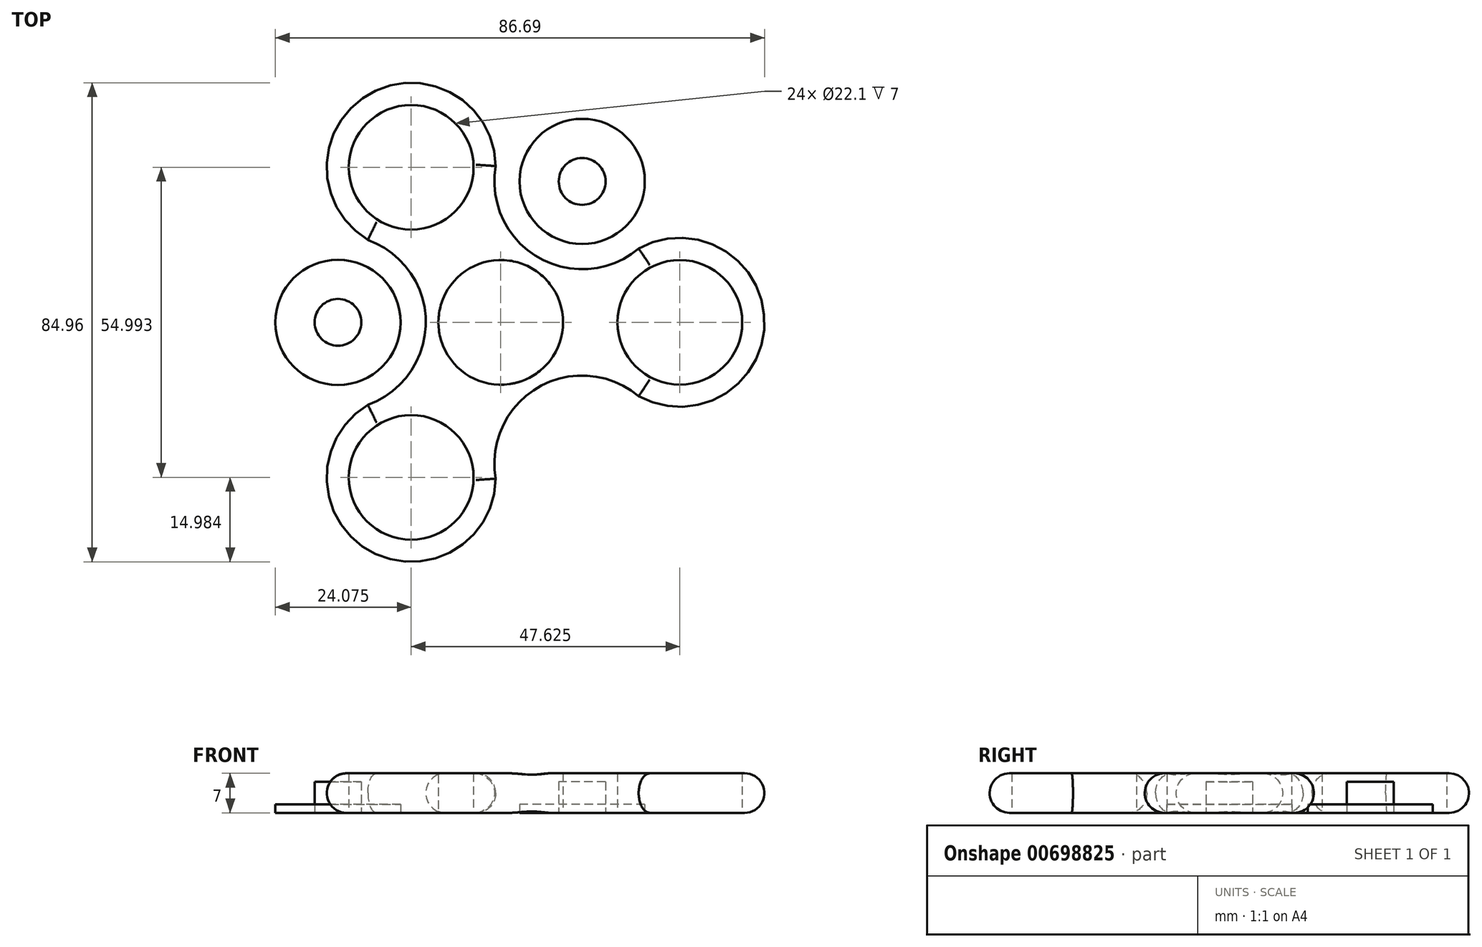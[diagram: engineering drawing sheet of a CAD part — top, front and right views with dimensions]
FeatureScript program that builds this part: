
annotation { "Feature Type Name" : "Feature", "Feature Type Description" : "" }
export const myFeature = defineFeature(function(context is Context, id is Id, definition is map)
    precondition{}
    {
        {
            var Q0;
            Q0=qCreatedBy(makeId("Top.planeOp"),FACE);
            var sketch = newSketch(context, id + "F0", { "sketchPlane" : qUnion([Q0])});
            skCircle(sketch, "E0", {"center": v(0, 0) * mm, "radius": 11.05 * mm});
            skCircle(sketch, "E1", {"center": v(0, 0) * mm, "radius": 14.99 * mm});
            skLineSegment(sketch, "E2", {"start": v(-11.05, 0) * mm, "end": v(-14.99, 0) * mm, "construction": true});
            skLineSegment(sketch, "E3.0", {"start": v(29.97, 0) * mm, "end": v(-14.99, -25.96) * mm, "construction": true});
            skLineSegment(sketch, "E3.1", {"start": v(-14.99, -25.96) * mm, "end": v(-14.99, 25.96) * mm, "construction": true});
            skLineSegment(sketch, "E3.2", {"start": v(-14.99, 25.96) * mm, "end": v(29.97, 0) * mm, "construction": true});
            skPoint(sketch, "E3.0.midPoint", {"position": v(7.5, -12.98) * mm});
            skLineSegment(sketch, "E4", {"start": v(0, 0) * mm, "end": v(7.5, 12.98) * mm, "construction": true});
            skLineSegment(sketch, "E5", {"start": v(0, 0) * mm, "end": v(7.5, -12.98) * mm, "construction": true});
            skLineSegment(sketch, "E6", {"start": v(0, 0) * mm, "end": v(-14.99, 0) * mm, "construction": true});
            skCircle(sketch, "E7", {"center": v(31.75, 0) * mm, "radius": 11.05 * mm});
            skLineSegment(sketch, "E8", {"start": v(42.8, 0) * mm, "end": v(46.74, 0) * mm, "construction": true});
            skLineSegment(sketch, "E9", {"start": v(31.75, 14.99) * mm, "end": v(31.75, -14.99) * mm, "construction": true});
            skLineSegment(sketch, "E10", {"start": v(0, 0) * mm, "end": v(31.75, 0) * mm, "construction": true});
            skCircle(sketch, "E11", {"center": v(31.75, 0) * mm, "radius": 14.99 * mm});
            skLineSegment(sketch, "E12", {"start": v(0, 0) * mm, "end": v(-15.88, 27.5) * mm, "construction": true});
            skCircle(sketch, "E13", {"center": v(-15.87, 27.5) * mm, "radius": 14.99 * mm});
            skCircle(sketch, "E14", {"center": v(-15.87, 27.5) * mm, "radius": 11.05 * mm});
            skLineSegment(sketch, "E15", {"start": v(-28.85, 20) * mm, "end": v(-2.9, 34.99) * mm, "construction": true});
            skLineSegment(sketch, "E16", {"start": v(-14.99, 0) * mm, "end": v(7.5, 12.98) * mm, "construction": true});
            skLineSegment(sketch, "E17", {"start": v(-14.99, 0) * mm, "end": v(7.5, -12.98) * mm, "construction": true});
            skLineSegment(sketch, "E18", {"start": v(7.5, -12.98) * mm, "end": v(7.5, 12.98) * mm, "construction": true});
            skLineSegment(sketch, "E19", {"start": v(0, 0) * mm, "end": v(-15.87, -27.5) * mm, "construction": true});
            skCircle(sketch, "E20", {"center": v(-15.87, -27.5) * mm, "radius": 14.99 * mm});
            skCircle(sketch, "E21", {"center": v(-15.87, -27.5) * mm, "radius": 11.05 * mm});
            skLineSegment(sketch, "E22", {"start": v(-2.9, -34.99) * mm, "end": v(-28.85, -20) * mm, "construction": true});
            skLineSegment(sketch, "E23", {"start": v(-28.85, 20) * mm, "end": v(-28.85, -20) * mm});
            skLineSegment(sketch, "E24", {"start": v(-2.9, -34.99) * mm, "end": v(31.75, -14.99) * mm});
            skLineSegment(sketch, "E25", {"start": v(31.75, 14.99) * mm, "end": v(-2.9, 34.99) * mm});
            skPoint(sketch, "E26", {"position": v(-28.85, 0) * mm});
            skPoint(sketch, "E27", {"position": v(14.43, 24.99) * mm});
            skCircle(sketch, "E28", {"center": v(-28.85, 0) * mm, "radius": 15.56 * mm});
            skCircle(sketch, "E29", {"center": v(14.43, 24.99) * mm, "radius": 15.56 * mm});
            skPoint(sketch, "E30", {"position": v(14.43, -24.99) * mm});
            skCircle(sketch, "E31", {"center": v(14.43, -24.99) * mm, "radius": 15.56 * mm});
            skSolve(sketch);
        }
        {
            var Q0;
            Q0=makeQuery(id+"F0.imprint","IMPRINT",FACE,{"disambiguationData":[TD([[makeQuery(id+"F0.imprint","IMPRINT",EDGE,{"derivedFrom":sQuery(id+"F0.wireOp",EDGE,"E14")}),-1.0]])]});
            var Q1;
            Q1=makeQuery(id+"F0.imprint","IMPRINT",FACE,{"disambiguationData":[TD([[makeQuery(id+"F0.imprint","IMPRINT",EDGE,{"derivedFrom":sQuery(id+"F0.wireOp",EDGE,"E1")}),-1.0]])]});
            var Q2;
            Q2=makeQuery(id+"F0.imprint","IMPRINT",FACE,{"disambiguationData":[TD([[makeQuery(id+"F0.imprint","IMPRINT",EDGE,{"derivedFrom":sQuery(id+"F0.wireOp",EDGE,"E7")}),-1.0]])]});
            var Q3;
            Q3=makeQuery(id+"F0.imprint","IMPRINT",FACE,{"disambiguationData":[TD([[makeQuery(id+"F0.imprint","IMPRINT",EDGE,{"derivedFrom":sQuery(id+"F0.wireOp",EDGE,"E21")}),-1.0]])]});
            var Q4;
            Q4=makeQuery(id+"F0.imprint","IMPRINT",FACE,{"disambiguationData":[TD([[makeQuery(id+"F0.imprint","IMPRINT",EDGE,{"derivedFrom":sQuery(id+"F0.wireOp",EDGE,"E0")}),-1.0]])]});
            extrude(context, id + "F1", {"entities" : qUnion([Q0, Q1, Q2, Q3, Q4]), "depth" : 7 * mm, "offsetDistance" : 25.4 * mm});
        }
        {
            var Q0;
            Q0=makeQuery(id+"F1.opExtrude","CAP_EDGE",EDGE,{"disambiguationData":[OSD([sQuery(id+"F0.wireOp",EDGE,"E13")])],"isStart":false});
            var Q1;
            Q1=makeQuery(id+"F1.opExtrude","CAP_EDGE",EDGE,{"disambiguationData":[OSD([sQuery(id+"F0.wireOp",EDGE,"E28")])],"isStart":false});
            var Q2;
            Q2=makeQuery(id+"F1.opExtrude","CAP_EDGE",EDGE,{"disambiguationData":[OSD([sQuery(id+"F0.wireOp",EDGE,"E20")])],"isStart":false});
            var Q3;
            Q3=makeQuery(id+"F1.opExtrude","CAP_EDGE",EDGE,{"disambiguationData":[OSD([sQuery(id+"F0.wireOp",EDGE,"E31")])],"isStart":false});
            var Q4;
            Q4=makeQuery(id+"F1.opExtrude","CAP_EDGE",EDGE,{"disambiguationData":[OSD([sQuery(id+"F0.wireOp",EDGE,"E11")])],"isStart":false});
            var Q5;
            Q5=makeQuery(id+"F1.opExtrude","CAP_EDGE",EDGE,{"disambiguationData":[OSD([sQuery(id+"F0.wireOp",EDGE,"E29")])],"isStart":false});
            var Q6;
            Q6=makeQuery(id+"F1.opExtrude","CAP_EDGE",EDGE,{"disambiguationData":[OSD([sQuery(id+"F0.wireOp",EDGE,"E20")])],"isStart":true});
            var Q7;
            Q7=makeQuery(id+"F1.opExtrude","CAP_EDGE",EDGE,{"disambiguationData":[OSD([sQuery(id+"F0.wireOp",EDGE,"E28")])],"isStart":true});
            var Q8;
            Q8=makeQuery(id+"F1.opExtrude","CAP_EDGE",EDGE,{"disambiguationData":[OSD([sQuery(id+"F0.wireOp",EDGE,"E13")])],"isStart":true});
            var Q9;
            Q9=makeQuery(id+"F1.opExtrude","CAP_EDGE",EDGE,{"disambiguationData":[OSD([sQuery(id+"F0.wireOp",EDGE,"E31")])],"isStart":true});
            var Q10;
            Q10=makeQuery(id+"F1.opExtrude","CAP_EDGE",EDGE,{"disambiguationData":[OSD([sQuery(id+"F0.wireOp",EDGE,"E11")])],"isStart":true});
            var Q11;
            Q11=makeQuery(id+"F1.opExtrude","CAP_EDGE",EDGE,{"disambiguationData":[OSD([sQuery(id+"F0.wireOp",EDGE,"E29")])],"isStart":true});
            fillet(context, id + "F2", {"entities" : qUnion([Q0, Q1, Q2, Q3, Q4, Q5, Q6, Q7, Q8, Q9, Q10, Q11]), "radius" : 3.5 * mm, "tangentPropagation" : true, "allowEdgeOverflow" : false});
        }
        {
            var Q0;
            Q0=qCreatedBy(makeId("Top.planeOp"),FACE);
            var sketch = newSketch(context, id + "F3", { "sketchPlane" : qUnion([Q0])});
            skCircle(sketch, "E32", {"center": v(-28.85, 0) * mm, "radius": 11.1 * mm});
            skCircle(sketch, "E33", {"center": v(14.43, 24.99) * mm, "radius": 11.1 * mm});
            skLineSegment(sketch, "E34", {"start": v(-15.87, -27.5) * mm, "end": v(18.93, 32.79) * mm, "construction": true});
            skCircle(sketch, "E35", {"center": v(-28.85, 0) * mm, "radius": 4.15 * mm});
            skCircle(sketch, "E36", {"center": v(14.43, 24.99) * mm, "radius": 4.15 * mm});
            skLineSegment(sketch, "E37", {"start": v(10.83, 27.06) * mm, "end": v(4.81, 30.54) * mm});
            skLineSegment(sketch, "E38", {"start": v(-24.7, 0) * mm, "end": v(-17.75, 0) * mm});
            skSolve(sketch);
        }
        {
            var Q0;
            Q0=makeQuery(id+"F3.imprint","IMPRINT",FACE,{"disambiguationData":[TD([[makeQuery(id+"F3.imprint","IMPRINT",EDGE,{"derivedFrom":sQuery(id+"F3.wireOp",EDGE,"E32")}),1.0]])]});
            var Q1;
            Q1=makeQuery(id+"F3.imprint","IMPRINT",FACE,{"disambiguationData":[TD([[makeQuery(id+"F3.imprint","IMPRINT",EDGE,{"derivedFrom":sQuery(id+"F3.wireOp",EDGE,"E33")}),1.0]])]});
            var Q2;
            Q2=makeQuery(id+"F3.imprint","IMPRINT",FACE,{"disambiguationData":[TD([[makeQuery(id+"F3.imprint","IMPRINT",EDGE,{"derivedFrom":sQuery(id+"F3.wireOp",EDGE,"E35")}),1.0]])]});
            var Q3;
            Q3=makeQuery(id+"F3.imprint","IMPRINT",FACE,{"disambiguationData":[TD([[makeQuery(id+"F3.imprint","IMPRINT",EDGE,{"derivedFrom":sQuery(id+"F3.wireOp",EDGE,"E36")}),1.0]])]});
            extrude(context, id + "F4", {"entities" : qUnion([Q0, Q1, Q2, Q3]), "depth" : 1.5 * mm, "offsetDistance" : 25.4 * mm});
        }
        {
            var Q0;
            Q0=makeQuery(id+"F3.imprint","IMPRINT",FACE,{"disambiguationData":[TD([[makeQuery(id+"F3.imprint","IMPRINT",EDGE,{"derivedFrom":sQuery(id+"F3.wireOp",EDGE,"E35")}),1.0]])]});
            var Q1;
            Q1=makeQuery(id+"F3.imprint","IMPRINT",FACE,{"disambiguationData":[TD([[makeQuery(id+"F3.imprint","IMPRINT",EDGE,{"derivedFrom":sQuery(id+"F3.wireOp",EDGE,"E36")}),1.0]])]});
            extrude(context, id + "F5", {"entities" : qUnion([Q0, Q1]), "depth" : 5.5 * mm, "offsetDistance" : 25.4 * mm});
        }
    });
